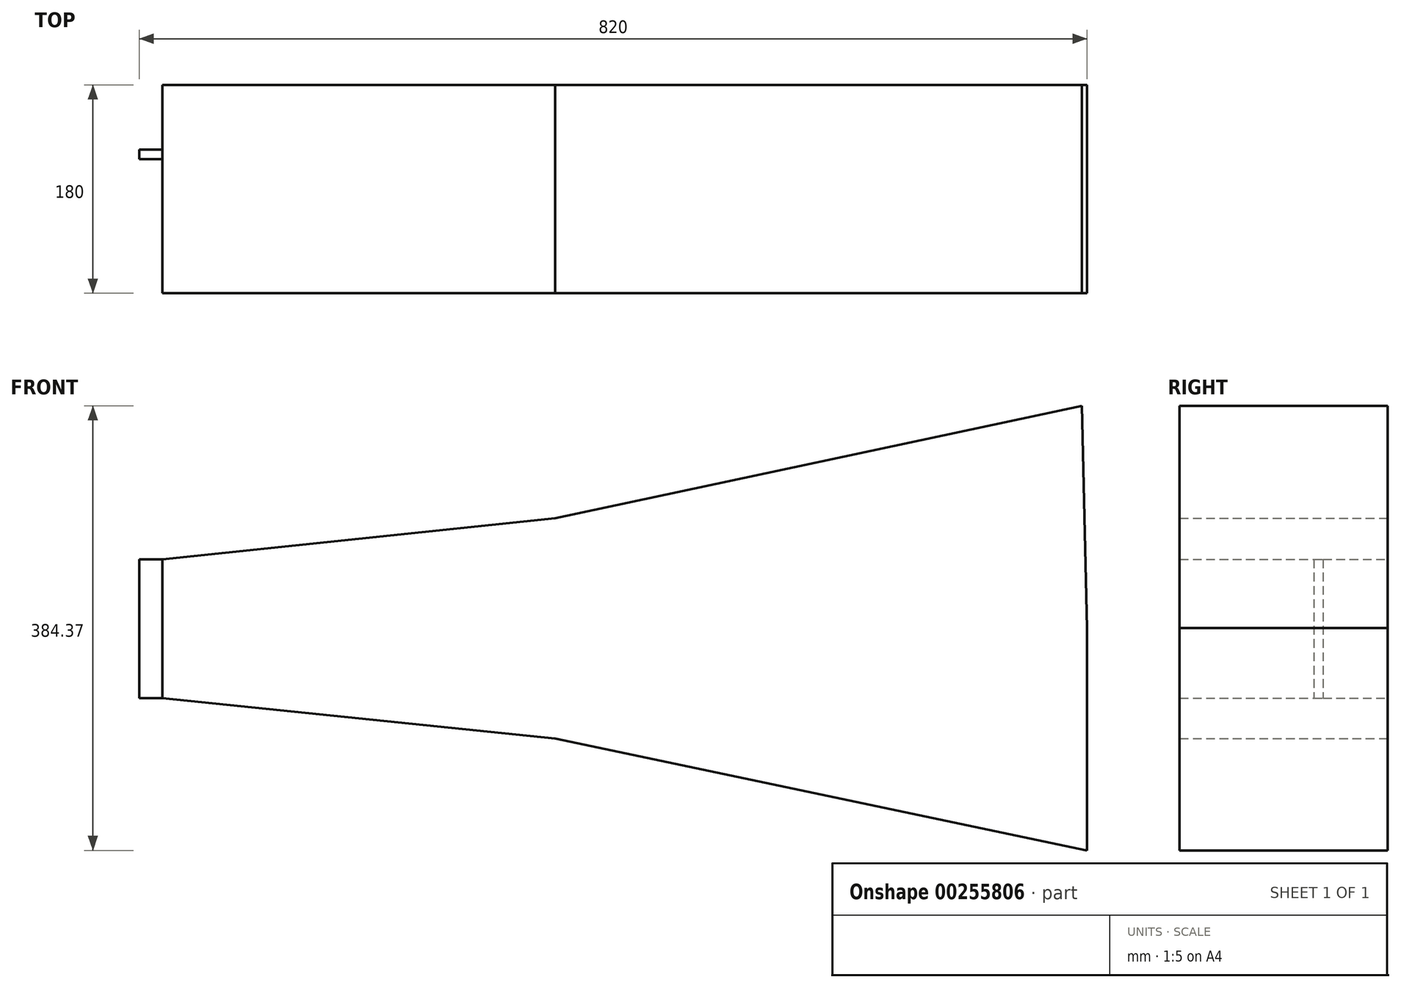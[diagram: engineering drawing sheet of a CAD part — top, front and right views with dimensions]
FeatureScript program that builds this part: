
annotation { "Feature Type Name" : "Feature", "Feature Type Description" : "" }
export const myFeature = defineFeature(function(context is Context, id is Id, definition is map)
    precondition{}
    {
        {
            var Q0;
            Q0=qCreatedBy(makeId("Front.planeOp"),FACE);
            var sketch = newSketch(context, id + "F0", { "sketchPlane" : qUnion([Q0])});
            skLineSegment(sketch, "E0", {"start": v(0, 0) * mm, "end": v(0, 60) * mm});
            skLineSegment(sketch, "E1", {"start": v(0, 0) * mm, "end": v(0, 0.07) * mm});
            skPoint(sketch, "E2.visualSharp", {"position": v(0, 0.57) * mm});
            skArc(sketch, "E2.filletArc", {"start": v(0.5, 0.57) * mm, "mid": v(0.15, 0.42) * mm, "end": v(0, 0.07) * mm});
            skLineSegment(sketch, "E3", {"start": v(0, 60) * mm, "end": v(340, 95.54) * mm});
            skLineSegment(sketch, "E4", {"start": v(340, 95.54) * mm, "end": v(795.5, 192.76) * mm});
            skLineSegment(sketch, "E5", {"start": v(0.5, 0.57) * mm, "end": v(800, 0.57) * mm});
            skLineSegment(sketch, "E6", {"start": v(795.5, 192.76) * mm, "end": v(800, 0.57) * mm});
            skLineSegment(sketch, "E7", {"start": v(800, 0.57) * mm, "end": v(800, -191.61) * mm});
            skLineSegment(sketch, "E8", {"start": v(340, 55.87) * mm, "end": v(340, 39.02) * mm});
            skLineSegment(sketch, "E9", {"start": v(340, 0) * mm, "end": v(340, -94.97) * mm});
            skLineSegment(sketch, "E10", {"start": v(340, -94.97) * mm, "end": v(800, -191.61) * mm});
            skLineSegment(sketch, "E11", {"start": v(0, -60) * mm, "end": v(340, -94.97) * mm});
            skLineSegment(sketch, "E12", {"start": v(0, -60) * mm, "end": v(0, 60) * mm});
            skSolve(sketch);
        }
        {
            var Q0;
            Q0=qSketchRegion(id+"F0",true);
            extrude(context, id + "F1", {"entities" : qUnion([Q0]), "depth" : 8 * mm, "offsetDistance" : 25 * mm, "symmetric" : true});
        }
        {
            var Q0;
            Q0 = qSketchRegion(id + "F0", true);
            extrude(context, id + "F2", {"entities" : qUnion([Q0]), "operationType" : NewBodyOperationType.ADD, "depth" : 120 * mm, "offsetDistance" : 25 * mm, "symmetric" : true});
        }
        {
            var Q0;
            Q0=makeQuery(id+"F2.opExtrude","CAP_FACE",FACE,{"disambiguationData":[OSD([sQuery(id+"F0.wireOp",EDGE,"E3"),sQuery(id+"F0.wireOp",EDGE,"E4"),sQuery(id+"F0.wireOp",EDGE,"E6"),sQuery(id+"F0.wireOp",EDGE,"CMODCZlB-PxfF-klAX-XbT7-CyTCxeAvkly6"),sQuery(id+"F0.wireOp",EDGE,"2GonKtnm-jUKS-e5YD-eOxZ-3jPt60j523Pc"),sQuery(id+"F0.wireOp",EDGE,"Mqq0Nyr2-VLej-06lk-Hiri-qnpPfLe2HBmq"),sQuery(id+"F0.wireOp",EDGE,"E7"),sQuery(id+"F0.wireOp",EDGE,"WS3j79eA-NCSG-McHF-mbzJ-VnLdKLQSw4Np"),sQuery(id+"F0.wireOp",EDGE,"E10")])],"isStart":false});
            extrude(context, id + "F3", {"entities" : qUnion([Q0]), "operationType" : NewBodyOperationType.ADD, "depth" : 120 * mm, "offsetDistance" : 25 * mm, "symmetric" : true});
        }
        {
            var Q0;
            Q0=qCreatedBy(makeId("Front.planeOp"),FACE);
            var sketch = newSketch(context, id + "F4", { "sketchPlane" : qUnion([Q0])});
            skLineSegment(sketch, "E13", {"start": v(0, 0) * mm, "end": v(-20, 0) * mm});
            skLineSegment(sketch, "E14", {"start": v(-20, 0) * mm, "end": v(-20, -60) * mm});
            skLineSegment(sketch, "E15.top", {"start": v(0, 60) * mm, "end": v(-20, 60) * mm});
            skLineSegment(sketch, "E15.left", {"start": v(0, 0) * mm, "end": v(0, 60) * mm});
            skLineSegment(sketch, "E16", {"start": v(-20, -60) * mm, "end": v(0, -60) * mm});
            skLineSegment(sketch, "E17", {"start": v(-20, 60) * mm, "end": v(-20, 0) * mm});
            skLineSegment(sketch, "E18.bottom", {"start": v(-20, 0) * mm, "end": v(0, 0) * mm});
            skLineSegment(sketch, "E18.right", {"start": v(0, 0) * mm, "end": v(0, -60) * mm});
            skSolve(sketch);
        }
        {
            var Q0;
            Q0 = qSketchRegion(id + "F4", true);
            extrude(context, id + "F5", {"entities" : qUnion([Q0]), "operationType" : NewBodyOperationType.ADD, "depth" : 8 * mm, "offsetDistance" : 25 * mm, "symmetric" : true});
        }
    });
